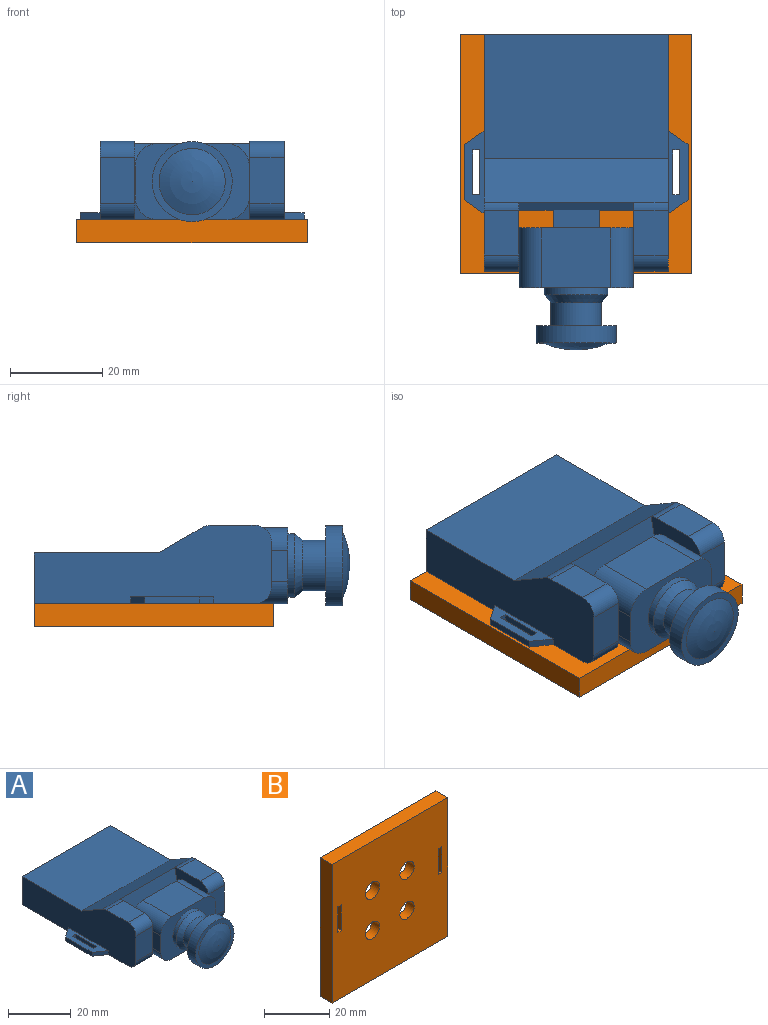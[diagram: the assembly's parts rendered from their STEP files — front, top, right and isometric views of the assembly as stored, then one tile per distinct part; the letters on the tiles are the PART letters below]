
ASSEMBLY  parts=2 mates=1
PART A: 57 faces, bbox 48.7x68.6x17.4 mm
  f0: plane 51.5x17mm, normal (-1,0,0), area 650.2mm2, adj f2,f3,f8,f9,f10,f11,f12,f13
  f1: cylinder r=3.5mm len=7.5mm, axis (-1,0,0), area 13.8mm2, adj f4,f11,f15,f17
  f2: plane 48.66x48mm, normal (0,0,-1), area 1733.3mm2, adj f0,f5,f8,f9,f15,f16,f17,f18
  f3: plane 10x7.5mm, normal (0,-1,0), area 75mm2, adj f0,f8,f14,f16
  f4: plane 9.74x7.5mm, normal (0,0,1), area 73.1mm2, adj f1,f6,f15,f17
  f5: cylinder r=3.5mm len=7.5mm, axis (-1,0,0), area 41.2mm2, adj f2,f7,f15,f17
  f6: cylinder r=3.5mm len=7.5mm, axis (-1,0,0), area 41.2mm2, adj f4,f7,f15,f17
  f7: plane 10x7.5mm, normal (0,-1,0), area 75mm2, adj f5,f6,f15,f17
  f8: cylinder r=3.5mm len=7.5mm, axis (-1,0,0), area 41.2mm2, adj f0,f2,f3,f16
  f9: plane 40x11mm, normal (0,1,0), area 440mm2, adj f0,f2,f10,f15
  f10: plane 40x27mm, normal (0,0,1), area 1080mm2, adj f0,f9,f11,f15
  f11: plane 40x9.5mm, normal (0,0.5,0.86), area 439.6mm2, adj f0,f1,f10,f12,f15,f19
  f12: cylinder r=3.5mm len=7.5mm, axis (-1,0,0), area 13.8mm2, adj f0,f11,f13,f16
  f13: plane 9.74x7.5mm, normal (0,0,1), area 73.1mm2, adj f0,f12,f14,f16
  f14: cylinder r=3.5mm len=7.5mm, axis (-1,0,0), area 41.2mm2, adj f0,f3,f13,f16
  f15: plane 51.5x17mm, normal (1,0,0), area 650.2mm2, adj f1,f2,f4,f5,f6,f7,f9,f10
  f16: plane 17x15mm, normal (1,0,0), area 234.9mm2, adj f2,f3,f8,f12,f13,f14,f18,f19
  f17: plane 17x15mm, normal (-1,0,0), area 234.9mm2, adj f1,f2,f4,f5,f6,f7,f18,f19
  f18: plane 25x8.5mm, normal (0,-0.98,-0.2), area 211.9mm2, adj f2,f16,f17,f19,f36,f37,f39
  f19: plane 25x8.03mm, normal (0,-0.98,0.21), area 200.3mm2, adj f11,f16,f17,f18,f37,f38,f39
  f20: plane 12x1.5mm, normal (-1,0,0), area 18mm2, adj f2,f21,f26,f27
  f21: plane 4.33x3mm, normal (-0.57,0.82,0), area 7.9mm2, adj f0,f2,f20,f27
  f22: plane 1.5x1.5mm, normal (0,-1,0), area 2.3mm2, adj f2,f23,f25,f27
  f23: plane 9.7x1.5mm, normal (1,0,0), area 14.6mm2, adj f2,f22,f24,f27
  f24: plane 1.5x1.5mm, normal (0,1,0), area 2.3mm2, adj f2,f23,f25,f27
  f25: plane 9.7x1.5mm, normal (-1,0,0), area 14.6mm2, adj f2,f22,f24,f27
  f26: plane 4.33x3mm, normal (-0.57,-0.82,0), area 7.9mm2, adj f0,f2,f20,f27
  f27: plane 18x4.33mm, normal (0,0,1), area 50.4mm2, adj f0,f20,f21,f22,f23,f24,f25,f26
  f28: plane 12x1.5mm, normal (1,0,0), area 18mm2, adj f2,f29,f34,f35
  f29: plane 4.33x3mm, normal (0.57,0.82,0), area 7.9mm2, adj f2,f15,f28,f35
  f30: plane 1.5x1.5mm, normal (0,-1,0), area 2.3mm2, adj f2,f31,f33,f35
  f31: plane 9.7x1.5mm, normal (-1,0,0), area 14.6mm2, adj f2,f30,f32,f35
  f32: plane 1.5x1.5mm, normal (0,1,0), area 2.3mm2, adj f2,f31,f33,f35
  f33: plane 9.7x1.5mm, normal (1,0,0), area 14.6mm2, adj f2,f30,f32,f35
  f34: plane 4.33x3mm, normal (0.57,-0.82,0), area 7.9mm2, adj f2,f15,f28,f35
  f35: plane 18x4.33mm, normal (0,0,1), area 50.4mm2, adj f15,f28,f29,f30,f31,f32,f33,f34
  f36: plane 10x3.94mm, normal (0,0,-1), area 39.4mm2, adj f18,f37,f39,f48
  f37: plane 3.95x1mm, normal (-1,0,0), area 3.9mm2, adj f18,f19,f36,f38,f48
  f38: plane 10x3.95mm, normal (0,0,1), area 39.5mm2, adj f19,f37,f39,f48
  f39: plane 3.95x1mm, normal (1,0,0), area 3.9mm2, adj f18,f19,f36,f38,f48
  f40: plane 13x6.73mm, normal (-1,0,0), area 87.4mm2, adj f41,f47,f48,f49
  f41: cylinder r=4.9mm len=13mm, axis (0,-1,0), area 100.1mm2, adj f40,f42,f48,f49
  f42: plane 15x13mm, normal (0,0,-1), area 195mm2, adj f41,f43,f48,f49
  f43: cylinder r=4.9mm len=13mm, axis (0,-1,0), area 100.1mm2, adj f42,f44,f48,f49
  f44: plane 13x6.73mm, normal (1,0,0), area 87.4mm2, adj f43,f45,f48,f49
  f45: cylinder r=4.9mm len=13mm, axis (0,-1,0), area 100.1mm2, adj f44,f46,f48,f49
  f46: plane 15x13mm, normal (0,0,1), area 195mm2, adj f45,f47,f48,f49
  f47: cylinder r=4.9mm len=13mm, axis (0,-1,0), area 100.1mm2, adj f40,f46,f48,f49
  f48: plane 24.8x16.53mm, normal (0,1,0), area 379.2mm2, adj f36,f37,f38,f39,f40,f41,f42,f43
  f49: plane 24.8x16.53mm, normal (0,-1,0), area 239.7mm2, adj f40,f41,f42,f43,f44,f45,f46,f47
  f50: sphere r=18.03mm, area 169.9mm2, adj f51
  f51: plane 17.4x17.4mm, normal (0,-1,0), area 74.9mm2, adj f50,f52
  f52: cylinder r=8.7mm len=17.4mm, axis (0,1,0), area 202.3mm2, adj f51,f53
  f53: plane 17.4x17.4mm, normal (0,1,0), area 142.8mm2, adj f52,f54
  f54: cylinder r=5.5mm len=11mm, axis (0,1,0), area 172.8mm2, adj f53,f55
  f55: cone r=5.5mm half-angle=37.9deg, axis (0,1,0), area 88.8mm2, adj f54,f56
  f56: cylinder r=6.9mm len=13.8mm, axis (0,1,0), area 65mm2, adj f49,f55
PART B: 26 faces, bbox 50x5x52 mm
  f0: plane 52x5mm, normal (1,0,0), area 260mm2, adj f1,f11,f12,f13
  f1: plane 50x5mm, normal (0,0,1), area 250mm2, adj f0,f2,f12,f13
  f2: plane 52x5mm, normal (-1,0,0), area 260mm2, adj f1,f11,f12,f13
  f3: plane 5x1.5mm, normal (0,0,1), area 7.5mm2, adj f4,f9,f12,f13
  f4: plane 9.7x5mm, normal (1,0,0), area 48.5mm2, adj f3,f5,f12,f13
  f5: plane 5x1.5mm, normal (0,0,-1), area 7.5mm2, adj f4,f9,f12,f13
  f6: plane 5x1.5mm, normal (0,0,1), area 7.5mm2, adj f7,f10,f12,f13
  f7: plane 9.7x5mm, normal (1,0,0), area 48.5mm2, adj f6,f8,f12,f13
  f8: plane 5x1.5mm, normal (0,0,-1), area 7.5mm2, adj f7,f10,f12,f13
  f9: plane 9.7x5mm, normal (-1,0,0), area 48.5mm2, adj f3,f5,f12,f13
  f10: plane 9.7x5mm, normal (-1,0,0), area 48.5mm2, adj f6,f8,f12,f13
  f11: plane 50x5mm, normal (0,0,-1), area 250mm2, adj f0,f2,f12,f13
  f12: plane 52x50mm, normal (0,-1,0), area 2451.1mm2, adj f0,f1,f2,f3,f4,f5,f6,f7
  f13: plane 52x50mm, normal (0,1,0), area 2130.3mm2, adj f0,f1,f2,f3,f4,f5,f6,f7
  f14: cylinder r=5.92mm len=11.84mm, axis (0,1,0), area 59.5mm2, adj f13,f15
  f15: plane 11.84x11.84mm, normal (0,1,0), area 80.2mm2, adj f14,f25
  f16: cylinder r=5.92mm len=11.84mm, axis (0,1,0), area 59.5mm2, adj f13,f17
  f17: plane 11.84x11.84mm, normal (0,1,0), area 80.2mm2, adj f16,f24
  f18: cylinder r=5.92mm len=11.84mm, axis (0,1,0), area 59.5mm2, adj f13,f19
  f19: plane 11.84x11.84mm, normal (0,1,0), area 80.2mm2, adj f18,f23
  f20: cylinder r=5.92mm len=11.84mm, axis (0,1,0), area 59.5mm2, adj f13,f21
  f21: plane 11.84x11.84mm, normal (0,1,0), area 80.2mm2, adj f20,f22
  f22: cylinder r=3.09mm len=6.18mm, axis (0,1,0), area 66mm2, adj f12,f21
  f23: cylinder r=3.09mm len=6.18mm, axis (0,1,0), area 66mm2, adj f12,f19
  f24: cylinder r=3.09mm len=6.18mm, axis (0,1,0), area 66mm2, adj f12,f17
  f25: cylinder r=3.09mm len=6.18mm, axis (0,1,0), area 66mm2, adj f12,f15
PLACE A t=(2.81,15.95,0.39)mm
PLACE B rot(axis=(0,-0.71,0.71),180deg) t=(2.78,15.7,-4.61)mm
MATE fastened B.f12 <-> A.f2  axis (0,0,1) through (25.28,6.85,0.39)mm
